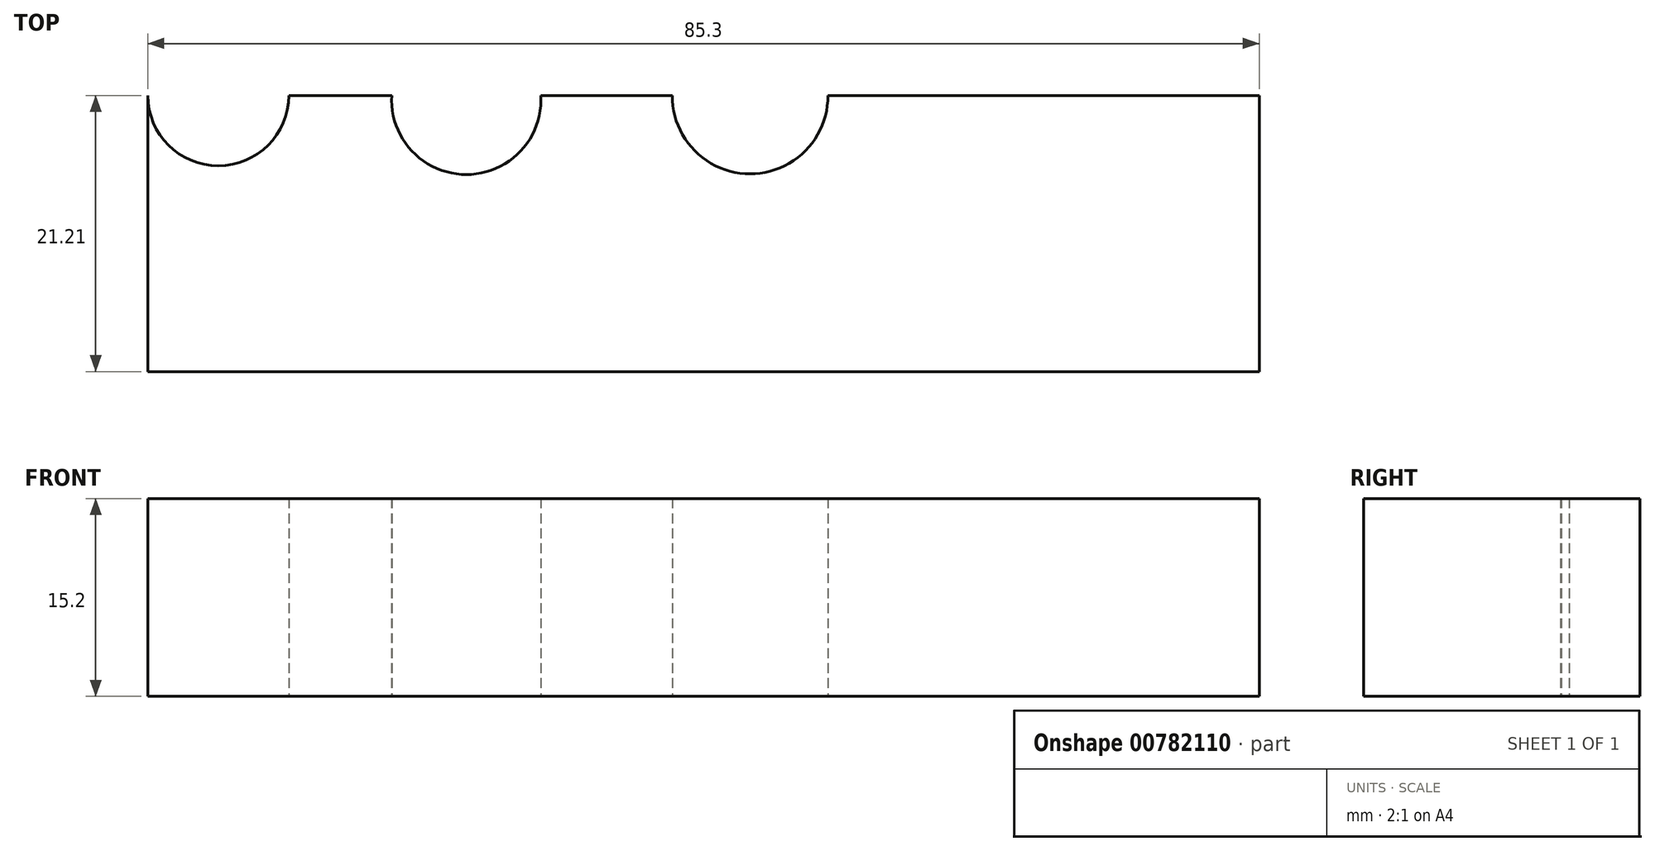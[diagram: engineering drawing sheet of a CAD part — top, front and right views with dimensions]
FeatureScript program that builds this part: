
annotation { "Feature Type Name" : "Feature", "Feature Type Description" : "" }
export const myFeature = defineFeature(function(context is Context, id is Id, definition is map)
    precondition{}
    {
        {
            var Q0;
            Q0=qCreatedBy(makeId("Front.planeOp"),FACE);
            var sketch = newSketch(context, id + "F0", { "sketchPlane" : qUnion([Q0])});
            skLineSegment(sketch, "E0.bottom", {"start": v(-85.3, 15.2) * mm, "end": v(0, 15.2) * mm});
            skLineSegment(sketch, "E0.top", {"start": v(-85.3, 0) * mm, "end": v(0, 0) * mm});
            skLineSegment(sketch, "E0.left", {"start": v(-85.3, 15.2) * mm, "end": v(-85.3, 0) * mm});
            skLineSegment(sketch, "E0.right", {"start": v(0, 15.2) * mm, "end": v(0, 0) * mm});
            skSolve(sketch);
        }
        {
            var Q0;
            Q0=makeQuery(id+"F0.imprint","IMPRINT",FACE,{"disambiguationData":[TD([[makeQuery(id+"F0.imprint","IMPRINT",EDGE,{"derivedFrom":sQuery(id+"F0.wireOp",EDGE,"E0.bottom")}),-1.0]])]});
            extrude(context, id + "F1", {"entities" : qUnion([Q0]), "depth" : 15 * mm, "offsetDistance" : 25 * mm});
        }
        {
            var Q0;
            Q0=qCreatedBy(makeId("Top.planeOp"),FACE);
            var sketch = newSketch(context, id + "F2", { "sketchPlane" : qUnion([Q0])});
            skLineSegment(sketch, "E1.bottom", {"start": v(-85.3, 0) * mm, "end": v(0, 0) * mm});
            skLineSegment(sketch, "E1.top", {"start": v(-85.3, 6.21) * mm, "end": v(0, 6.21) * mm});
            skLineSegment(sketch, "E1.left", {"start": v(-85.3, 0) * mm, "end": v(-85.3, 6.21) * mm});
            skLineSegment(sketch, "E1.right", {"start": v(0, 0) * mm, "end": v(0, 6.21) * mm});
            skArc(sketch, "E2", {"start": v(-85.3, 6.21) * mm, "mid": v(-79.9, 0.8) * mm, "end": v(-74.49, 6.21) * mm});
            skArc(sketch, "E3", {"start": v(-66.58, 6.21) * mm, "mid": v(-60.86, 0.14) * mm, "end": v(-55.14, 6.21) * mm});
            skArc(sketch, "E4", {"start": v(-45.05, 6.21) * mm, "mid": v(-39.07, 0.2) * mm, "end": v(-33.1, 6.21) * mm});
            skSolve(sketch);
        }
        {
            var Q0;
            Q0=makeQuery(id+"F2.imprint","IMPRINT",FACE,{"disambiguationData":[TD([[makeQuery(id+"F2.imprint","IMPRINT",EDGE,{"derivedFrom":sQuery(id+"F2.wireOp",EDGE,"E1.bottom")}),1.0]])]});
            extrude(context, id + "F3", {"entities" : qUnion([Q0]), "operationType" : NewBodyOperationType.ADD, "depth" : 15.2 * mm, "offsetDistance" : 25 * mm});
        }
    });
